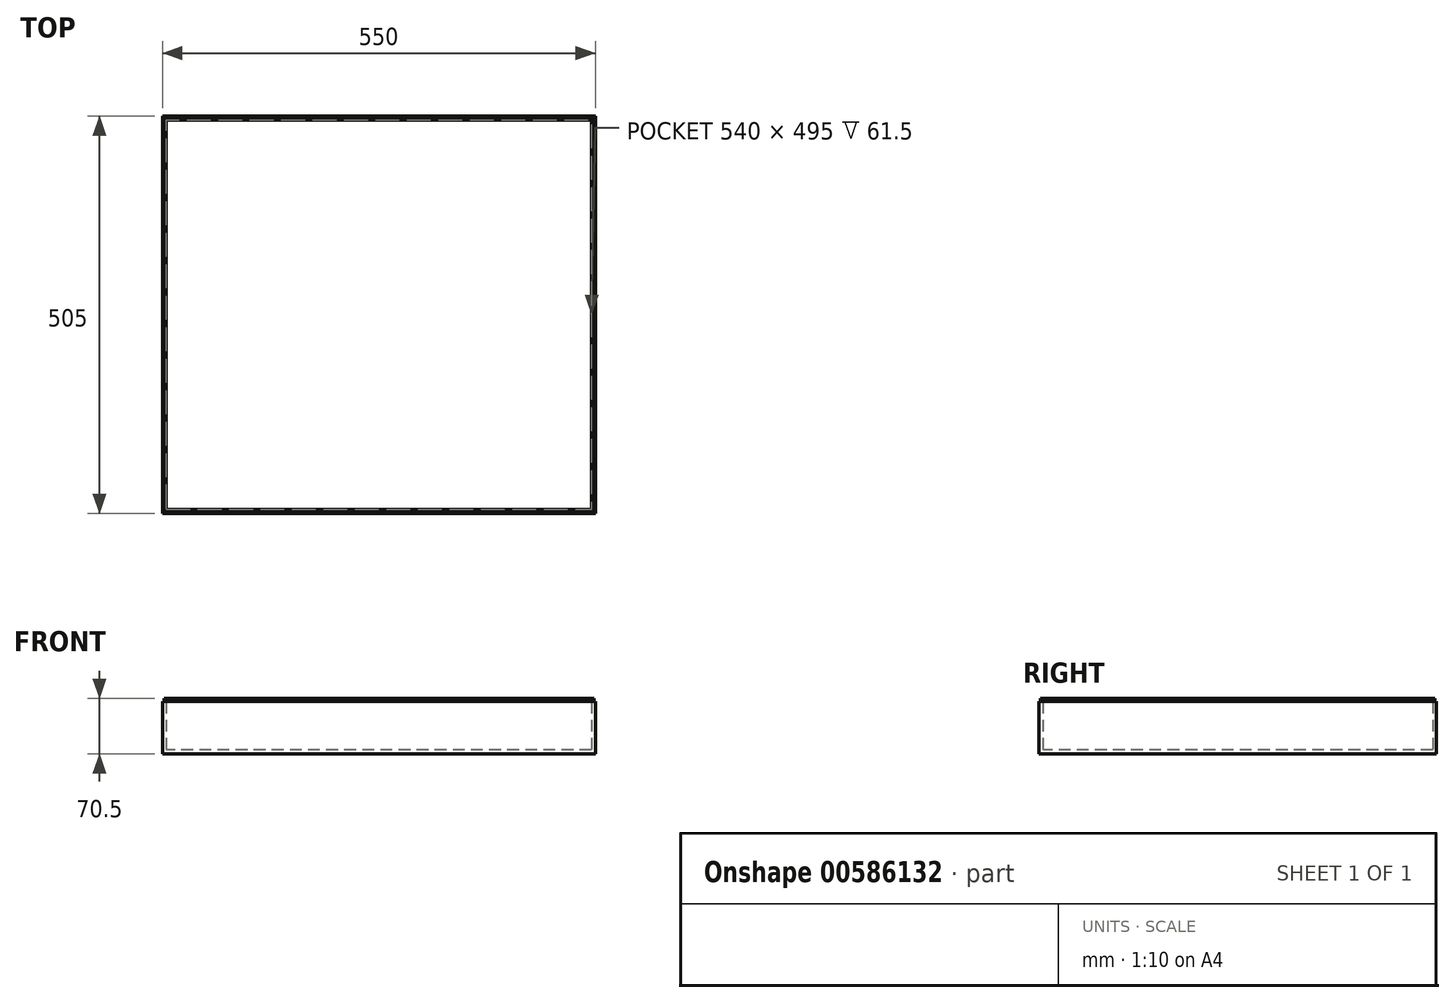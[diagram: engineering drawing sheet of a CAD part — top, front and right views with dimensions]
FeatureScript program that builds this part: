
annotation { "Feature Type Name" : "Feature", "Feature Type Description" : "" }
export const myFeature = defineFeature(function(context is Context, id is Id, definition is map)
    precondition{}
    {
        {
            var Q0;
            Q0=qCreatedBy(makeId("Top.planeOp"),FACE);
            var sketch = newSketch(context, id + "F0", { "sketchPlane" : qUnion([Q0])});
            skLineSegment(sketch, "E0.bottom", {"start": v(275, 252.5) * mm, "end": v(-275, 252.5) * mm});
            skLineSegment(sketch, "E0.top", {"start": v(275, -252.5) * mm, "end": v(-275, -252.5) * mm});
            skLineSegment(sketch, "E0.left", {"start": v(275, 252.5) * mm, "end": v(275, -252.5) * mm});
            skLineSegment(sketch, "E0.right", {"start": v(-275, 252.5) * mm, "end": v(-275, -252.5) * mm});
            skPoint(sketch, "E0.middle", {"position": v(0, 0) * mm});
            skSolve(sketch);
        }
        {
            var Q0;
            Q0 = qSketchRegion(id + "F0", true);
            extrude(context, id + "F1", {"entities" : qUnion([Q0]), "depth" : 5 * mm, "offsetDistance" : 25.4 * mm});
        }
        {
            var Q0;
            Q0=makeQuery(id+"F1.opExtrude","CAP_FACE",FACE,{"disambiguationData":[OSD([sQuery(id+"F0.wireOp",EDGE,"E0.bottom"),sQuery(id+"F0.wireOp",EDGE,"E0.top"),sQuery(id+"F0.wireOp",EDGE,"E0.left"),sQuery(id+"F0.wireOp",EDGE,"E0.right")])],"isStart":false});
            var sketch = newSketch(context, id + "F2", { "sketchPlane" : qUnion([Q0])});
            skLineSegment(sketch, "E1.bottom", {"start": v(275, -252.5) * mm, "end": v(-275, -252.5) * mm});
            skLineSegment(sketch, "E1.top", {"start": v(275, 252.5) * mm, "end": v(-275, 252.5) * mm});
            skLineSegment(sketch, "E1.left", {"start": v(275, -252.5) * mm, "end": v(275, 252.5) * mm});
            skLineSegment(sketch, "E1.right", {"start": v(-275, -252.5) * mm, "end": v(-275, 252.5) * mm});
            skPoint(sketch, "E1.middle", {"position": v(0, 0) * mm});
            skLineSegment(sketch, "E2.bottom", {"start": v(-275, -252.5) * mm, "end": v(-270, -252.5) * mm});
            skLineSegment(sketch, "E2.left", {"start": v(-275, -252.5) * mm, "end": v(-275, -247.5) * mm});
            skLineSegment(sketch, "E3.bottom", {"start": v(275, 252.5) * mm, "end": v(270, 252.5) * mm});
            skLineSegment(sketch, "E3.left", {"start": v(275, 252.5) * mm, "end": v(275, 247.5) * mm});
            skLineSegment(sketch, "E4.bottom", {"start": v(270, 247.5) * mm, "end": v(-270, 247.5) * mm});
            skLineSegment(sketch, "E4.top", {"start": v(270, -247.5) * mm, "end": v(-270, -247.5) * mm});
            skLineSegment(sketch, "E4.left", {"start": v(270, 247.5) * mm, "end": v(270, -247.5) * mm});
            skLineSegment(sketch, "E4.right", {"start": v(-270, 247.5) * mm, "end": v(-270, -247.5) * mm});
            skSolve(sketch);
        }
        {
            var Q0;
            Q0=makeQuery(id+"F2.imprint","IMPRINT",FACE,{"disambiguationData":[TD([[makeQuery(id+"F2.imprint","IMPRINT",EDGE,{"derivedFrom":sQuery(id+"F2.wireOp",EDGE,"E1.bottom")}),-1.0]])]});
            extrude(context, id + "F3", {"entities" : qUnion([Q0]), "operationType" : NewBodyOperationType.ADD, "depth" : 63.5 * mm - 2 * mm, "offsetDistance" : 25.4 * mm});
        }
        {
            var Q0;
            Q0=makeQuery(id+"F3.opExtrude","CAP_FACE",FACE,{"disambiguationData":[OSD([sQuery(id+"F2.wireOp",EDGE,"E1.bottom"),sQuery(id+"F2.wireOp",EDGE,"E1.top"),sQuery(id+"F2.wireOp",EDGE,"E1.left"),sQuery(id+"F2.wireOp",EDGE,"E1.right"),sQuery(id+"F2.wireOp",EDGE,"E2.bottom"),sQuery(id+"F2.wireOp",EDGE,"E2.left"),sQuery(id+"F2.wireOp",EDGE,"E3.bottom"),sQuery(id+"F2.wireOp",EDGE,"E3.left"),sQuery(id+"F2.wireOp",EDGE,"E4.bottom"),sQuery(id+"F2.wireOp",EDGE,"E4.top"),sQuery(id+"F2.wireOp",EDGE,"E4.left"),sQuery(id+"F2.wireOp",EDGE,"E4.right")])],"isStart":false});
            var sketch = newSketch(context, id + "F4", { "sketchPlane" : qUnion([Q0])});
            skLineSegment(sketch, "E5.bottom", {"start": v(-270, -247.5) * mm, "end": v(-271, -247.5) * mm});
            skLineSegment(sketch, "E5.top", {"start": v(-270, -248.5) * mm, "end": v(-271, -248.5) * mm});
            skLineSegment(sketch, "E5.left", {"start": v(-270, -247.5) * mm, "end": v(-270, -248.5) * mm});
            skLineSegment(sketch, "E5.right", {"start": v(-271, -247.5) * mm, "end": v(-271, -248.5) * mm});
            skLineSegment(sketch, "E6.bottom", {"start": v(270, 247.5) * mm, "end": v(271, 247.5) * mm});
            skLineSegment(sketch, "E6.top", {"start": v(270, 248.5) * mm, "end": v(271, 248.5) * mm});
            skLineSegment(sketch, "E6.left", {"start": v(270, 247.5) * mm, "end": v(270, 248.5) * mm});
            skLineSegment(sketch, "E6.right", {"start": v(271, 247.5) * mm, "end": v(271, 248.5) * mm});
            skLineSegment(sketch, "E7.top", {"start": v(271, 250.5) * mm, "end": v(273, 250.5) * mm});
            skLineSegment(sketch, "E7.right", {"start": v(273, 248.5) * mm, "end": v(273, 250.5) * mm});
            skLineSegment(sketch, "E8.top", {"start": v(-273, -250.5) * mm, "end": v(-276, -250.5) * mm});
            skLineSegment(sketch, "E8.right", {"start": v(-273, -248.5) * mm, "end": v(-273, -250.5) * mm});
            skLineSegment(sketch, "E9.bottom", {"start": v(-271, -248.5) * mm, "end": v(271, -248.5) * mm});
            skLineSegment(sketch, "E9.top", {"start": v(-271, 248.5) * mm, "end": v(271, 248.5) * mm});
            skLineSegment(sketch, "E9.left", {"start": v(-271, -248.5) * mm, "end": v(-271, 248.5) * mm});
            skLineSegment(sketch, "E9.right", {"start": v(271, -248.5) * mm, "end": v(271, 248.5) * mm});
            skLineSegment(sketch, "E10.bottom", {"start": v(273, 250.5) * mm, "end": v(-273, 250.5) * mm});
            skLineSegment(sketch, "E10.top", {"start": v(273, -250.5) * mm, "end": v(-273, -250.5) * mm});
            skLineSegment(sketch, "E10.left", {"start": v(273, 250.5) * mm, "end": v(273, -250.5) * mm});
            skLineSegment(sketch, "E10.right", {"start": v(-273, 250.5) * mm, "end": v(-273, -250.5) * mm});
            skSolve(sketch);
        }
        {
            var Q0;
            Q0 = qSketchRegion(id + "F4", true);
            extrude(context, id + "F5", {"entities" : qUnion([Q0]), "operationType" : NewBodyOperationType.ADD, "depth" : 4 * mm, "offsetDistance" : 25.4 * mm});
        }
        {
            var Q0;
            Q0=makeQuery(id+"F5.opExtrude","SWEPT_FACE",FACE,{"disambiguationData":[OSD([sQuery(id+"F4.wireOp",EDGE,"E10.top")])]});
            var sketch = newSketch(context, id + "F6", { "sketchPlane" : qUnion([Q0])});
            skLineSegment(sketch, "E11.left", {"start": v(-33.51, 69.5) * mm, "end": v(-33.51, 71.5) * mm});
            skLineSegment(sketch, "E11.right", {"start": v(33.51, 69.5) * mm, "end": v(33.51, 71.5) * mm});
            skPoint(sketch, "E11.middle", {"position": v(0, 70.5) * mm});
            skLineSegment(sketch, "E12.bottom", {"start": v(0, 70.5) * mm, "end": v(-1.5, 70.5) * mm});
            skLineSegment(sketch, "E13.bottom", {"start": v(-1.5, 70.5) * mm, "end": v(-4.5, 70.5) * mm});
            skLineSegment(sketch, "E14.bottom", {"start": v(0, 70.5) * mm, "end": v(1.5, 70.5) * mm});
            skLineSegment(sketch, "E15.bottom", {"start": v(1.5, 70.5) * mm, "end": v(4.5, 70.5) * mm});
            skArc(sketch, "E16", {"start": v(-5.5, 69.5) * mm, "mid": v(-4.5, 68.5) * mm, "end": v(-3.5, 69.5) * mm});
            skArc(sketch, "E17", {"start": v(-2.5, 69.5) * mm, "mid": v(-1.5, 68.5) * mm, "end": v(-0.5, 69.5) * mm});
            skArc(sketch, "E18", {"start": v(0.5, 69.5) * mm, "mid": v(1.5, 68.5) * mm, "end": v(2.5, 69.5) * mm});
            skArc(sketch, "E19", {"start": v(3.5, 69.5) * mm, "mid": v(4.5, 68.5) * mm, "end": v(5.5, 69.5) * mm});
            skLineSegment(sketch, "E20", {"start": v(-5.5, 69.5) * mm, "end": v(-5.5, 70.5) * mm});
            skLineSegment(sketch, "E21", {"start": v(-3.5, 69.5) * mm, "end": v(-3.5, 70.5) * mm});
            skLineSegment(sketch, "E22", {"start": v(-2.5, 69.5) * mm, "end": v(-2.5, 70.5) * mm});
            skLineSegment(sketch, "E23", {"start": v(-0.5, 69.5) * mm, "end": v(-0.5, 70.5) * mm});
            skLineSegment(sketch, "E24", {"start": v(0.5, 69.5) * mm, "end": v(0.5, 70.5) * mm});
            skLineSegment(sketch, "E25", {"start": v(2.5, 69.5) * mm, "end": v(2.5, 70.5) * mm});
            skLineSegment(sketch, "E26", {"start": v(3.5, 69.5) * mm, "end": v(3.5, 70.5) * mm});
            skLineSegment(sketch, "E27", {"start": v(5.5, 69.5) * mm, "end": v(5.5, 70.5) * mm});
            skLineSegment(sketch, "E28", {"start": v(-5.5, 70.5) * mm, "end": v(-4.5, 70.5) * mm});
            skSolve(sketch);
        }
        {
            var Q0;
            Q0=makeQuery(id+"F6.imprint","IMPRINT",FACE,{"disambiguationData":[TD([[makeQuery(id+"F6.imprint","IMPRINT",EDGE,{"derivedFrom":sQuery(id+"F6.wireOp",EDGE,"E19")}),1.0]])]});
            var Q1;
            Q1=makeQuery(id+"F6.imprint","IMPRINT",FACE,{"disambiguationData":[TD([[makeQuery(id+"F6.imprint","IMPRINT",EDGE,{"derivedFrom":sQuery(id+"F6.wireOp",EDGE,"E18")}),1.0]])]});
            var Q2;
            Q2=makeQuery(id+"F6.imprint","IMPRINT",FACE,{"disambiguationData":[TD([[makeQuery(id+"F6.imprint","IMPRINT",EDGE,{"derivedFrom":sQuery(id+"F6.wireOp",EDGE,"E16")}),1.0]])]});
            var Q3;
            Q3=makeQuery(id+"F6.imprint","IMPRINT",FACE,{"disambiguationData":[TD([[makeQuery(id+"F6.imprint","IMPRINT",EDGE,{"derivedFrom":sQuery(id+"F6.wireOp",EDGE,"E17")}),1.0]])]});
            extrude(context, id + "F7", {"entities" : qUnion([Q0, Q1, Q2, Q3]), "operationType" : NewBodyOperationType.REMOVE, "oppositeDirection" : true, "depth" : 25.4 * mm, "offsetDistance" : 25.4 * mm});
        }
    });
